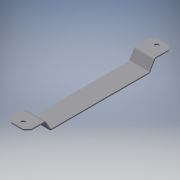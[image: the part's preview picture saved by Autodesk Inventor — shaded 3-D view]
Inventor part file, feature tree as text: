
AUTODESK INVENTOR PART (.ipt)
format: ipt  version: 2016 (Build 200138000, 138)  size: 157,696 bytes
history: native  units: mm
features: sheet_metal_op x7, other x4, sketch x4, hole x1, reference x1
ambient origin geometry x8: Origin, YZ Plane, XZ Plane, XY Plane, X Axis, Y Axis, Z Axis, Center Point
bodies: Solid1 (feature_tree)
feature tree (17):
  sheet_metal_op  "Face1"
  sheet_metal_op  "Flange1"
  sheet_metal_op  "Flange2"
  other  "Corner Chamfer1"
  hole  "Hole1"  [1 undecoded]
  sketch  "Sketch1"  dims[d0=100.0mm d1=20.0mm]
  other  "Plate1"
  sketch  "Sketch2"  dims[d3=1.2mm]
  other  "Plate2"
  sheet_metal_op  "Bend1"
  sheet_metal_op  "Corner1"
  sketch  "Sketch3"  dims[d4=1.2mm]
  other  "Plate3"
  sheet_metal_op  "Bend2"
  sheet_metal_op  "Corner2"
  sketch  "Sketch4"  dims[d5=0.6mm d6=2.4mm d7=1.2mm d8=12.0mm d9=60.0deg d10=1.2mm d11=4.8mm d12=1.2mm d13=1.2mm d14=1.2mm d15=0.6mm d16=2.4mm d17=1.2mm d18=18.0mm d19=60.0deg d20=1.2mm d21=4.8mm d22=1.2mm d23=1.2mm d24=4.0mm d25=6.0mm d26=45.0deg d27=6.0mm d28=6.0mm d29=4.2mm d30=6.0mm d31=4.0mm d32=2.0mm d33=90.0deg d34=1.2mm d35=20.594885mm d36=45.0mm]
  reference  "Reference1"
note: 1 required parameter value undecoded (feature->parameter linkage not recoverable at this tier; creation-order binding heuristic only, values carry confidence <= 0.55)
